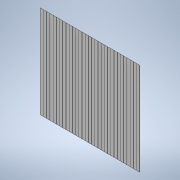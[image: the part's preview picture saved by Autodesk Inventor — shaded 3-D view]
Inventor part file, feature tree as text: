
AUTODESK INVENTOR PART (.ipt)
format: ipt  version: 2021 (Build 250183000, 183)  size: 225,792 bytes
history: native  units: in
note: dims shown in document units (in); Inventor stores cm internally (conversion verified against a paired STEP export)
features: extrude x3, sketch x3, pattern_linear x1, projected_geometry x1
ambient origin geometry x8: Origin, YZ Plane, XZ Plane, XY Plane, X Axis, Y Axis, Z Axis, Center Point
bodies: Solid1 (feature_tree)
feature tree (8):
  extrude  "Extrusion1"  Depth=3.0in
  extrude  "Extrusion2"  Depth=0.1in
  pattern_linear  "Rectangular Pattern1"  Count1=31 Spacing1=0.104in
  extrude  "Extrusion3"  Depth=0.104in TaperAngle=0.0deg
  sketch  "Sketch1"  dims[d0=4.0in d1=3.0in]
  sketch  "Sketch2"  dims[d2=0.04in d3=0.0in d4=0.1in]
  projected_geometry  "Projected Loop1"
  sketch  "Sketch3"  dims[d5=0.0015in d6=0.0in d7=12.2047in d9=0.104in d10=1.0in d11=0.0in]
